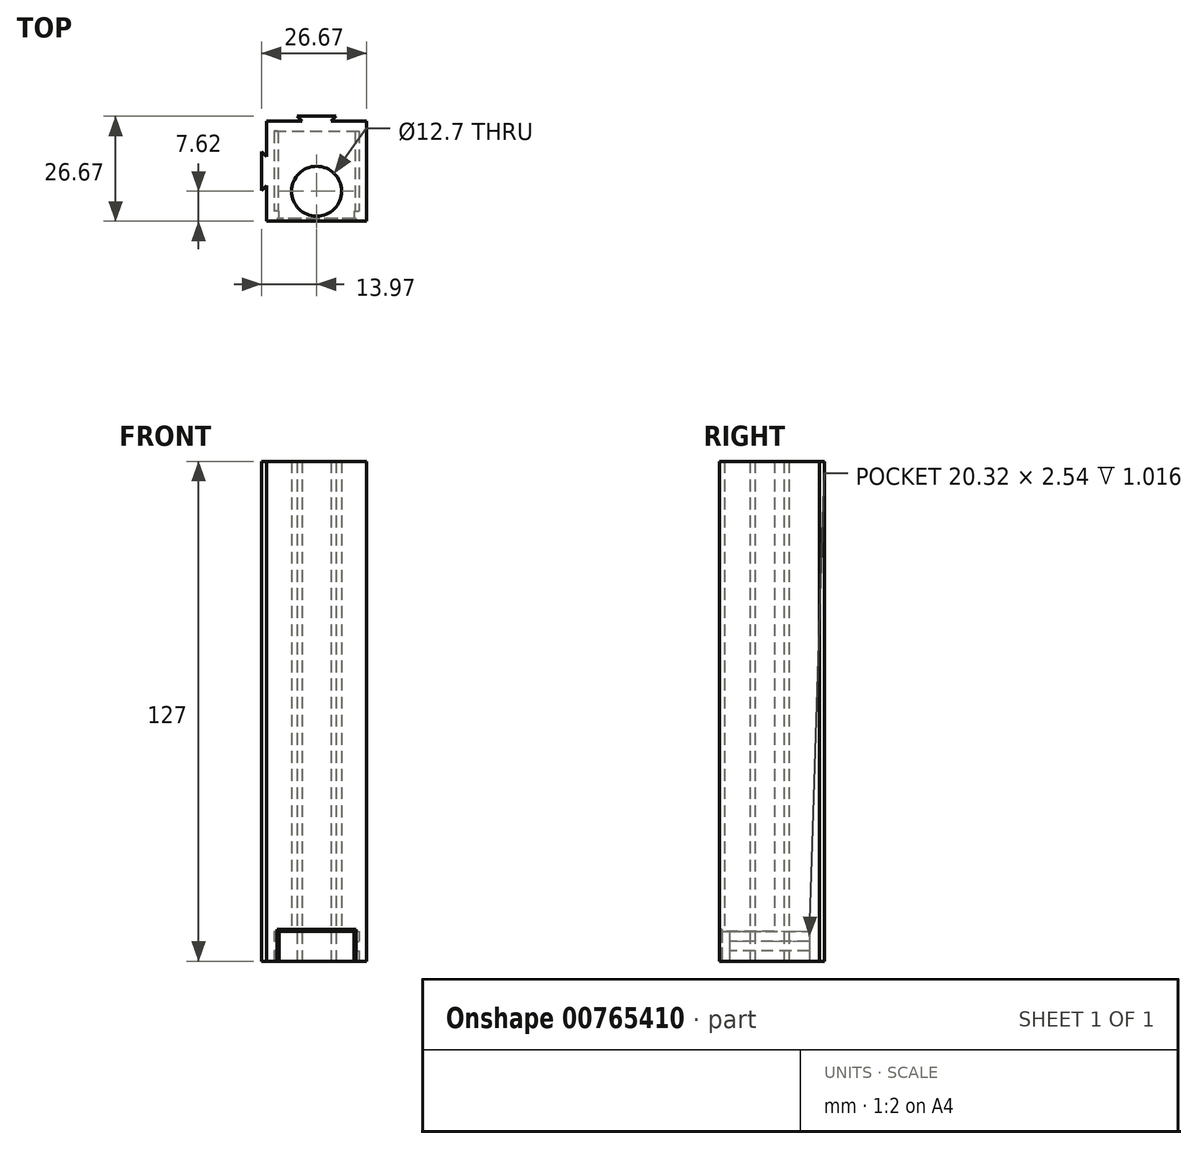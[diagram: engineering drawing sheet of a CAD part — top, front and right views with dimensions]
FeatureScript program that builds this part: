
annotation { "Feature Type Name" : "Feature", "Feature Type Description" : "" }
export const myFeature = defineFeature(function(context is Context, id is Id, definition is map)
    precondition{}
    {
        {
            var Q0;
            Q0=qCreatedBy(makeId("Top.planeOp"),FACE);
            var sketch = newSketch(context, id + "F0", { "sketchPlane" : qUnion([Q0])});
            skLineSegment(sketch, "E0.bottom", {"start": v(12.7, 12.7) * mm, "end": v(-12.7, 12.7) * mm});
            skLineSegment(sketch, "E0.top", {"start": v(12.7, -12.7) * mm, "end": v(-12.7, -12.7) * mm});
            skLineSegment(sketch, "E0.left", {"start": v(12.7, 12.7) * mm, "end": v(12.7, -12.7) * mm});
            skLineSegment(sketch, "E0.right", {"start": v(-12.7, 12.7) * mm, "end": v(-12.7, -12.7) * mm});
            skPoint(sketch, "E0.middle", {"position": v(0, 0) * mm});
            skLineSegment(sketch, "E1", {"start": v(-3.68, 12.7) * mm, "end": v(-4.95, 13.97) * mm});
            skLineSegment(sketch, "E2", {"start": v(-4.95, 13.97) * mm, "end": v(4.95, 13.97) * mm});
            skLineSegment(sketch, "E3", {"start": v(4.95, 13.97) * mm, "end": v(3.68, 12.7) * mm});
            skLineSegment(sketch, "E4.MirrorCS", {"start": v(-12.7, 3.68) * mm, "end": v(-13.97, 4.95) * mm});
            skLineSegment(sketch, "E5.MirrorCS", {"start": v(-13.97, 4.95) * mm, "end": v(-13.97, -4.95) * mm});
            skLineSegment(sketch, "E6.MirrorCS", {"start": v(-13.97, -4.95) * mm, "end": v(-12.7, -3.68) * mm});
            skCircle(sketch, "E7", {"center": v(0, -5.08) * mm, "radius": 6.35 * mm});
            skSolve(sketch);
        }
        {
            var Q0;
            Q0=makeQuery(id+"F0.imprint","IMPRINT",FACE,{"disambiguationData":[TD([[makeQuery(id+"F0.imprint","IMPRINT",EDGE,{"derivedFrom":sQuery(id+"F0.wireOp",EDGE,"E7")}),-1.0]])]});
            var Q1;
            {var subQ0=sQuery(id+"F0.wireOp",EDGE,"E4.MirrorCS");Q1=makeQuery(id+"F0.imprint","IMPRINT",FACE,{"disambiguationData":[TD([[makeQuery(id+"F0.imprint","IMPRINT",EDGE,{"derivedFrom":subQ0}),1.0]])]});}
            var Q2;
            {var subQ0=sQuery(id+"F0.wireOp",EDGE,"648ae852-5b30-4ce4-b5d7-663e1538fe900.MirrorCS");Q2=makeQuery(id+"F0.imprint","IMPRINT",FACE,{"disambiguationData":[TD([[makeQuery(id+"F0.imprint","IMPRINT",EDGE,{"derivedFrom":subQ0}),1.0]])]});}
            var Q3;
            {var subQ0=sQuery(id+"F0.wireOp",EDGE,"995b501b-87b1-40df-89db-5718103b703a");Q3=makeQuery(id+"F0.imprint","IMPRINT",FACE,{"disambiguationData":[TD([[makeQuery(id+"F0.imprint","IMPRINT",EDGE,{"derivedFrom":subQ0}),-1.0]])]});}
            var Q4;
            {var subQ0=sQuery(id+"F0.wireOp",EDGE,"E1");Q4=makeQuery(id+"F0.imprint","IMPRINT",FACE,{"disambiguationData":[TD([[makeQuery(id+"F0.imprint","IMPRINT",EDGE,{"derivedFrom":subQ0}),-1.0]])]});}
            extrude(context, id + "F1", {"entities" : qUnion([Q0, Q1, Q2, Q3, Q4]), "depth" : 127 * mm, "offsetDistance" : 25.4 * mm});
        }
        {
            var Q0;
            Q0=makeQuery(id+"F1.opExtrude","CAP_FACE",FACE,{"disambiguationData":[OSD([sQuery(id+"F0.wireOp",EDGE,"E0.bottom"),sQuery(id+"F0.wireOp",EDGE,"E0.top"),sQuery(id+"F0.wireOp",EDGE,"E0.left"),sQuery(id+"F0.wireOp",EDGE,"E0.right"),sQuery(id+"F0.wireOp",EDGE,"E1"),sQuery(id+"F0.wireOp",EDGE,"E2"),sQuery(id+"F0.wireOp",EDGE,"E3"),sQuery(id+"F0.wireOp",EDGE,"995b501b-87b1-40df-89db-5718103b703a"),sQuery(id+"F0.wireOp",EDGE,"d9b632a0-34b0-463a-8696-1e9d1799fc8a"),sQuery(id+"F0.wireOp",EDGE,"b3bc504c-1797-48d5-8887-40c9249a8113"),sQuery(id+"F0.wireOp",EDGE,"E4.MirrorCS"),sQuery(id+"F0.wireOp",EDGE,"E5.MirrorCS"),sQuery(id+"F0.wireOp",EDGE,"E6.MirrorCS"),sQuery(id+"F0.wireOp",EDGE,"E7")])],"isStart":true});
            var sketch = newSketch(context, id + "F2", { "sketchPlane" : qUnion([Q0])});
            skLineSegment(sketch, "E8", {"start": v(-9.52, 12.7) * mm, "end": v(-9.52, 10.16) * mm});
            skLineSegment(sketch, "E9", {"start": v(-9.52, 10.16) * mm, "end": v(-10.8, 10.16) * mm});
            skLineSegment(sketch, "E10", {"start": v(-10.8, 10.16) * mm, "end": v(-10.8, -10.16) * mm});
            skLineSegment(sketch, "E11", {"start": v(-10.8, -10.16) * mm, "end": v(10.8, -10.16) * mm});
            skLineSegment(sketch, "E12", {"start": v(10.8, -10.16) * mm, "end": v(10.8, 10.16) * mm});
            skLineSegment(sketch, "E13", {"start": v(9.52, 10.16) * mm, "end": v(10.8, 10.16) * mm});
            skLineSegment(sketch, "E14", {"start": v(9.52, 10.16) * mm, "end": v(9.52, 12.7) * mm});
            skLineSegment(sketch, "E15", {"start": v(9.52, 12.7) * mm, "end": v(-9.52, 12.7) * mm});
            skSolve(sketch);
        }
        {
            var Q0;
            Q0=makeQuery(id+"F2.imprint","IMPRINT",FACE,{"disambiguationData":[TD([[makeQuery(id+"F2.imprint","IMPRINT",EDGE,{"derivedFrom":sQuery(id+"F2.wireOp",EDGE,"E8")}),1.0]])]});
            extrude(context, id + "F3", {"entities" : qUnion([Q0]), "operationType" : NewBodyOperationType.REMOVE, "oppositeDirection" : true, "depth" : 7.62 * mm, "offsetDistance" : 25.4 * mm});
        }
        {
            var Q0;
            Q0=makeQuery(id+"F1.opExtrude","SWEPT_FACE",FACE,{"disambiguationData":[OSD([sQuery(id+"F0.wireOp",EDGE,"E0.top")])]});
            var sketch = newSketch(context, id + "F4", { "sketchPlane" : qUnion([Q0])});
            skLineSegment(sketch, "E16.0", {"start": v(-10.03, 8.13) * mm, "end": v(-10.03, 0) * mm});
            skLineSegment(sketch, "E16.1", {"start": v(10.03, 8.13) * mm, "end": v(-10.03, 8.13) * mm});
            skLineSegment(sketch, "E16.2", {"start": v(10.03, 8.13) * mm, "end": v(10.03, 0) * mm});
            skSolve(sketch);
        }
        {
            var Q0;
            {var subQ13=sQuery(id+"F4.wireOp",EDGE,"E16.0");Q0=makeQuery(id+"F4.imprint","IMPRINT",FACE,{"disambiguationData":[TD([[makeQuery(id+"F4.imprint","IMPRINT",EDGE,{"derivedFrom":subQ13}),1.0]])]});}
            extrude(context, id + "F5", {"entities" : qUnion([Q0]), "operationType" : NewBodyOperationType.REMOVE, "oppositeDirection" : true, "depth" : 0.64 * mm, "offsetDistance" : 25.4 * mm});
        }
        {
            var Q0;
            Q0=makeQuery(id+"F3.boolean.opBoolean","COPY",FACE,{"derivedFrom":makeQuery(id+"F3.opExtrude","SWEPT_FACE",FACE,{"disambiguationData":[OSD([sQuery(id+"F2.wireOp",EDGE,"E10")])]})});
            var sketch = newSketch(context, id + "F6", { "sketchPlane" : qUnion([Q0])});
            skLineSegment(sketch, "E17.bottom", {"start": v(10.16, 5.08) * mm, "end": v(-10.16, 5.08) * mm});
            skLineSegment(sketch, "E17.top", {"start": v(10.16, 2.67) * mm, "end": v(-10.16, 2.67) * mm});
            skLineSegment(sketch, "E17.left", {"start": v(10.16, 5.08) * mm, "end": v(10.16, 2.67) * mm});
            skLineSegment(sketch, "E17.right", {"start": v(-10.16, 5.08) * mm, "end": v(-10.16, 2.67) * mm});
            skSolve(sketch);
        }
        {
            var Q0;
            Q0=makeQuery(id+"F6.imprint","IMPRINT",FACE,{"disambiguationData":[TD([[makeQuery(id+"F6.imprint","IMPRINT",EDGE,{"derivedFrom":sQuery(id+"F6.wireOp",EDGE,"E17.bottom")}),1.0]])]});
            extrude(context, id + "F7", {"entities" : qUnion([Q0]), "depth" : 1.02 * mm, "offsetDistance" : 25.4 * mm});
        }
        {
            var Q0;
            Q0=makeQuery(id+"F7.opExtrude","SWEPT_BODY",BODY,{"disambiguationData":[OSD([sQuery(id+"F6.wireOp",EDGE,"E17.bottom"),sQuery(id+"F6.wireOp",EDGE,"E17.top"),sQuery(id+"F6.wireOp",EDGE,"E17.left"),sQuery(id+"F6.wireOp",EDGE,"E17.right")])]});
            var Q1;
            Q1=qCreatedBy(makeId("Right.planeOp"),FACE);
            mirror(context, id + "F8", {"operationType" : NewBodyOperationType.ADD, "entities" : qUnion([Q0]), "mirrorPlane" : qUnion([Q1])});
        }
        {
            var Q0;
            Q0=makeQuery(id+"F1.opExtrude","SWEPT_BODY",BODY,{"disambiguationData":[OSD([sQuery(id+"F0.wireOp",EDGE,"E0.bottom"),sQuery(id+"F0.wireOp",EDGE,"E0.top"),sQuery(id+"F0.wireOp",EDGE,"E0.left"),sQuery(id+"F0.wireOp",EDGE,"E0.right"),sQuery(id+"F0.wireOp",EDGE,"E1"),sQuery(id+"F0.wireOp",EDGE,"E2"),sQuery(id+"F0.wireOp",EDGE,"E3"),sQuery(id+"F0.wireOp",EDGE,"995b501b-87b1-40df-89db-5718103b703a"),sQuery(id+"F0.wireOp",EDGE,"d9b632a0-34b0-463a-8696-1e9d1799fc8a"),sQuery(id+"F0.wireOp",EDGE,"b3bc504c-1797-48d5-8887-40c9249a8113"),sQuery(id+"F0.wireOp",EDGE,"E4.MirrorCS"),sQuery(id+"F0.wireOp",EDGE,"E5.MirrorCS"),sQuery(id+"F0.wireOp",EDGE,"E6.MirrorCS"),sQuery(id+"F0.wireOp",EDGE,"E7")])]});
            transform(context, id + "F9", {"entities" : qUnion([Q0]), "transformType" : TransformType.TRANSLATION_3D, "dx" : 0 * mm, "dy" : 0 * mm, "dz" : 0 * mm, "makeCopy" : true});
        }
        {
            var Q0;
            Q0=makeQuery(id+"F9.opPattern","COPY",BODY,{"derivedFrom":makeQuery(id+"F1.opExtrude","SWEPT_BODY",BODY,{"disambiguationData":[OSD([sQuery(id+"F0.wireOp",EDGE,"E0.bottom"),sQuery(id+"F0.wireOp",EDGE,"E0.top"),sQuery(id+"F0.wireOp",EDGE,"E0.left"),sQuery(id+"F0.wireOp",EDGE,"E0.right"),sQuery(id+"F0.wireOp",EDGE,"E1"),sQuery(id+"F0.wireOp",EDGE,"E2"),sQuery(id+"F0.wireOp",EDGE,"E3"),sQuery(id+"F0.wireOp",EDGE,"995b501b-87b1-40df-89db-5718103b703a"),sQuery(id+"F0.wireOp",EDGE,"d9b632a0-34b0-463a-8696-1e9d1799fc8a"),sQuery(id+"F0.wireOp",EDGE,"b3bc504c-1797-48d5-8887-40c9249a8113"),sQuery(id+"F0.wireOp",EDGE,"E4.MirrorCS"),sQuery(id+"F0.wireOp",EDGE,"E5.MirrorCS"),sQuery(id+"F0.wireOp",EDGE,"E6.MirrorCS"),sQuery(id+"F0.wireOp",EDGE,"E7")])]}),"instanceName":"1"});
            deleteBodies(context, id + "F10", {"entities" : qUnion([Q0])});
        }
    });
